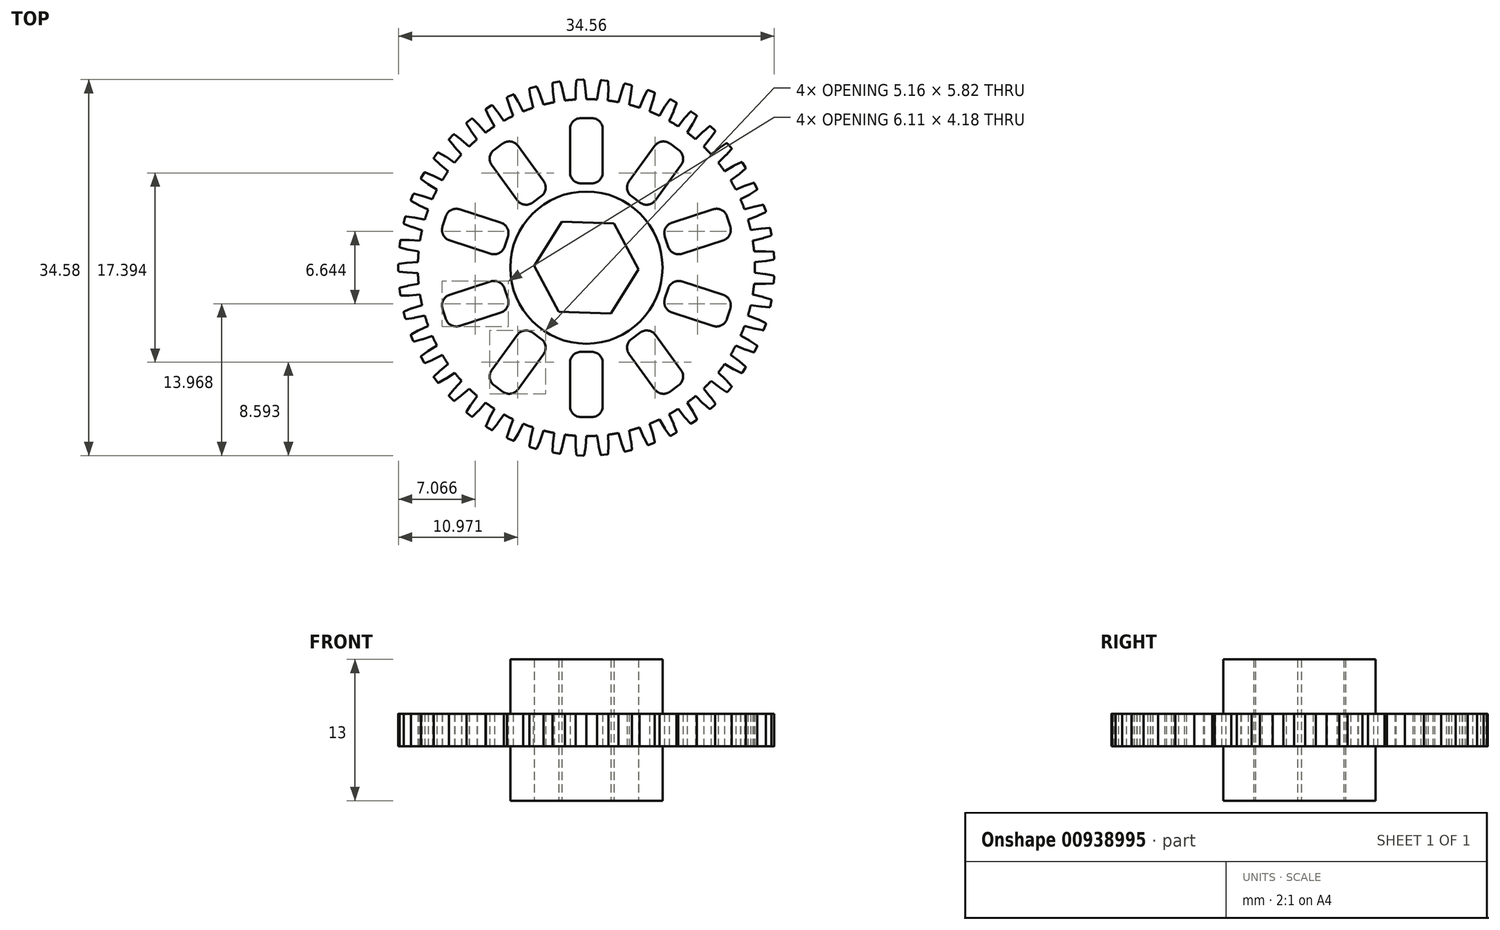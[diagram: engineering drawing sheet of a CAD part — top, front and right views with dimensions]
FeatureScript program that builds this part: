
annotation { "Feature Type Name" : "Feature", "Feature Type Description" : "" }
export const myFeature = defineFeature(function(context is Context, id is Id, definition is map)
    precondition{}
    {
        {
            var Q0;
            Q0=qCreatedBy(makeId("Top.planeOp"),FACE);
            var sketch = newSketch(context, id + "F0", { "sketchPlane" : qUnion([Q0])});
            skCircle(sketch, "E0", {"center": v(0, 0) * mm, "radius": 7 * mm});
            skArc(sketch, "E1", {"start": v(-1, 15.47) * mm, "mid": v(0.5, -15.5) * mm, "end": v(0, 15.5) * mm});
            skCircle(sketch, "E2", {"center": v(0, 0) * mm, "radius": 14.5 * mm});
            skLineSegment(sketch, "E3", {"start": v(-1, 15.47) * mm, "end": v(0, 15.5) * mm});
            skPoint(sketch, "E4.0.midPoint", {"position": v(-3.35, 1.99) * mm});
            skCircle(sketch, "E5.cCircle", {"center": v(0, 0) * mm, "radius": 4.15 * mm, "construction": true});
            skLineSegment(sketch, "E5.0", {"start": v(-4.79, 0.17) * mm, "end": v(-2.25, 4.23) * mm});
            skLineSegment(sketch, "E5.1", {"start": v(-2.25, 4.23) * mm, "end": v(2.54, 4.06) * mm});
            skLineSegment(sketch, "E5.2", {"start": v(2.54, 4.06) * mm, "end": v(4.79, -0.17) * mm});
            skLineSegment(sketch, "E5.3", {"start": v(4.79, -0.17) * mm, "end": v(2.25, -4.23) * mm});
            skLineSegment(sketch, "E5.4", {"start": v(2.25, -4.23) * mm, "end": v(-2.54, -4.06) * mm});
            skLineSegment(sketch, "E5.5", {"start": v(-2.54, -4.06) * mm, "end": v(-4.79, 0.17) * mm});
            skPoint(sketch, "E5.0.midPoint", {"position": v(-3.52, 2.2) * mm});
            skPoint(sketch, "E6.orphan", {"position": v(-2.3, -3.87) * mm});
            skPoint(sketch, "E7.orphan", {"position": v(2.2, -3.92) * mm});
            skPoint(sketch, "E8.orphan", {"position": v(-4.5, 0.05) * mm});
            skPoint(sketch, "E4.1.start.orphan", {"position": v(-2.2, 3.92) * mm});
            skLineSegment(sketch, "E9", {"start": v(-0.5, 15.48) * mm, "end": v(-0.53, 16.48) * mm});
            skLineSegment(sketch, "E10", {"start": v(-0.53, 16.48) * mm, "end": v(-0.98, 16.47) * mm});
            skLineSegment(sketch, "E11", {"start": v(-0.98, 16.47) * mm, "end": v(-0.08, 16.5) * mm});
            skLineSegment(sketch, "E12", {"start": v(-0.98, 16.45) * mm, "end": v(-1, 15.47) * mm});
            skLineSegment(sketch, "E13", {"start": v(-0.08, 16.48) * mm, "end": v(0, 15.5) * mm});
            skLineSegment(sketch, "E14", {"start": v(-0.53, 16.48) * mm, "end": v(-0.56, 17.28) * mm});
            skLineSegment(sketch, "E15", {"start": v(-0.56, 17.28) * mm, "end": v(-0.82, 17.27) * mm});
            skLineSegment(sketch, "E16", {"start": v(-0.82, 17.27) * mm, "end": v(-0.3, 17.3) * mm});
            skLineSegment(sketch, "E17", {"start": v(-0.92, 17.18) * mm, "end": v(-0.98, 16.49) * mm});
            skLineSegment(sketch, "E18", {"start": v(-0.2, 17.2) * mm, "end": v(-0.09, 16.52) * mm});
            skPoint(sketch, "E19.visualSharp", {"position": v(-0.2, 17.3) * mm});
            skArc(sketch, "E19.filletArc", {"start": v(-0.2, 17.2) * mm, "mid": v(-0.23, 17.27) * mm, "end": v(-0.3, 17.3) * mm});
            skPoint(sketch, "E20.visualSharp", {"position": v(-0.9, 17.27) * mm});
            skArc(sketch, "E20.filletArc", {"start": v(-0.82, 17.27) * mm, "mid": v(-0.88, 17.25) * mm, "end": v(-0.92, 17.18) * mm});
            skPoint(sketch, "E21.visualSharp", {"position": v(-0.08, 16.5) * mm});
            skArc(sketch, "E21.filletArc", {"start": v(-0.08, 16.48) * mm, "mid": v(-0.08, 16.5) * mm, "end": v(-0.09, 16.52) * mm});
            skPoint(sketch, "E22.visualSharp", {"position": v(-0.98, 16.47) * mm});
            skArc(sketch, "E22.filletArc", {"start": v(-0.98, 16.49) * mm, "mid": v(-0.98, 16.47) * mm, "end": v(-0.98, 16.45) * mm});
            skPoint(sketch, "E23", {"position": v(0, 7) * mm});
            skPoint(sketch, "E24", {"position": v(0, 14.5) * mm});
            skPoint(sketch, "E25", {"position": v(0, 10.75) * mm});
            skLineSegment(sketch, "E26.bottom", {"start": v(0.5, 13.75) * mm, "end": v(-0.5, 13.75) * mm});
            skLineSegment(sketch, "E26.top", {"start": v(0.5, 7.75) * mm, "end": v(-0.5, 7.75) * mm});
            skLineSegment(sketch, "E26.left", {"start": v(1.5, 12.75) * mm, "end": v(1.5, 8.75) * mm});
            skLineSegment(sketch, "E26.right", {"start": v(-1.5, 12.75) * mm, "end": v(-1.5, 8.75) * mm});
            skPoint(sketch, "E27.visualSharp", {"position": v(-1.5, 13.75) * mm});
            skArc(sketch, "E27.filletArc", {"start": v(-0.5, 13.75) * mm, "mid": v(-1.2, 13.46) * mm, "end": v(-1.5, 12.75) * mm});
            skPoint(sketch, "E28.visualSharp", {"position": v(1.5, 13.75) * mm});
            skArc(sketch, "E28.filletArc", {"start": v(1.5, 12.75) * mm, "mid": v(1.2, 13.46) * mm, "end": v(0.5, 13.75) * mm});
            skPoint(sketch, "E29.visualSharp", {"position": v(1.5, 7.75) * mm});
            skArc(sketch, "E29.filletArc", {"start": v(0.5, 7.75) * mm, "mid": v(1.2, 8.04) * mm, "end": v(1.5, 8.75) * mm});
            skPoint(sketch, "E30.visualSharp", {"position": v(-1.5, 7.75) * mm});
            skArc(sketch, "E30.filletArc", {"start": v(-1.5, 8.75) * mm, "mid": v(-1.2, 8.04) * mm, "end": v(-0.5, 7.75) * mm});
            skLineSegment(sketch, "E31.1.0", {"start": v(-7.68, 11.42) * mm, "end": v(-8.49, 10.83) * mm});
            skArc(sketch, "E31.1.1", {"start": v(-6.28, 11.2) * mm, "mid": v(-6.93, 11.6) * mm, "end": v(-7.68, 11.42) * mm});
            skLineSegment(sketch, "E31.1.2", {"start": v(-6.28, 11.2) * mm, "end": v(-3.93, 7.96) * mm});
            skArc(sketch, "E31.1.3", {"start": v(-4.15, 6.56) * mm, "mid": v(-3.75, 7.22) * mm, "end": v(-3.93, 7.96) * mm});
            skLineSegment(sketch, "E31.1.4", {"start": v(-4.15, 6.56) * mm, "end": v(-4.96, 5.98) * mm});
            skArc(sketch, "E31.1.5", {"start": v(-6.36, 6.2) * mm, "mid": v(-5.7, 5.8) * mm, "end": v(-4.96, 5.98) * mm});
            skLineSegment(sketch, "E31.1.6", {"start": v(-8.7, 9.43) * mm, "end": v(-6.36, 6.2) * mm});
            skArc(sketch, "E31.1.7", {"start": v(-8.49, 10.83) * mm, "mid": v(-8.89, 10.18) * mm, "end": v(-8.7, 9.43) * mm});
            skLineSegment(sketch, "E31.2.0", {"start": v(-12.92, 4.72) * mm, "end": v(-13.23, 3.77) * mm});
            skArc(sketch, "E31.2.1", {"start": v(-11.66, 5.37) * mm, "mid": v(-12.43, 5.3) * mm, "end": v(-12.92, 4.72) * mm});
            skLineSegment(sketch, "E31.2.2", {"start": v(-11.66, 5.37) * mm, "end": v(-7.86, 4.13) * mm});
            skArc(sketch, "E31.2.3", {"start": v(-7.22, 2.87) * mm, "mid": v(-7.28, 3.63) * mm, "end": v(-7.86, 4.13) * mm});
            skLineSegment(sketch, "E31.2.4", {"start": v(-7.22, 2.87) * mm, "end": v(-7.53, 1.92) * mm});
            skArc(sketch, "E31.2.5", {"start": v(-8.79, 1.28) * mm, "mid": v(-8.02, 1.34) * mm, "end": v(-7.53, 1.92) * mm});
            skLineSegment(sketch, "E31.2.6", {"start": v(-12.59, 2.51) * mm, "end": v(-8.79, 1.28) * mm});
            skArc(sketch, "E31.2.7", {"start": v(-13.23, 3.77) * mm, "mid": v(-13.17, 3.01) * mm, "end": v(-12.59, 2.51) * mm});
            skLineSegment(sketch, "E31.3.0", {"start": v(-13.23, -3.77) * mm, "end": v(-12.92, -4.72) * mm});
            skArc(sketch, "E31.3.1", {"start": v(-12.59, -2.51) * mm, "mid": v(-13.17, -3.01) * mm, "end": v(-13.23, -3.77) * mm});
            skLineSegment(sketch, "E31.3.2", {"start": v(-12.59, -2.51) * mm, "end": v(-8.79, -1.28) * mm});
            skArc(sketch, "E31.3.3", {"start": v(-7.53, -1.92) * mm, "mid": v(-8.02, -1.34) * mm, "end": v(-8.79, -1.28) * mm});
            skLineSegment(sketch, "E31.3.4", {"start": v(-7.53, -1.92) * mm, "end": v(-7.22, -2.87) * mm});
            skArc(sketch, "E31.3.5", {"start": v(-7.86, -4.13) * mm, "mid": v(-7.28, -3.63) * mm, "end": v(-7.22, -2.87) * mm});
            skLineSegment(sketch, "E31.3.6", {"start": v(-11.66, -5.37) * mm, "end": v(-7.86, -4.13) * mm});
            skArc(sketch, "E31.3.7", {"start": v(-12.92, -4.72) * mm, "mid": v(-12.43, -5.3) * mm, "end": v(-11.66, -5.37) * mm});
            skLineSegment(sketch, "E31.4.0", {"start": v(-8.49, -10.83) * mm, "end": v(-7.68, -11.42) * mm});
            skArc(sketch, "E31.4.1", {"start": v(-8.7, -9.43) * mm, "mid": v(-8.89, -10.18) * mm, "end": v(-8.49, -10.83) * mm});
            skLineSegment(sketch, "E31.4.2", {"start": v(-8.7, -9.43) * mm, "end": v(-6.36, -6.2) * mm});
            skArc(sketch, "E31.4.3", {"start": v(-4.96, -5.98) * mm, "mid": v(-5.7, -5.8) * mm, "end": v(-6.36, -6.2) * mm});
            skLineSegment(sketch, "E31.4.4", {"start": v(-4.96, -5.98) * mm, "end": v(-4.15, -6.56) * mm});
            skArc(sketch, "E31.4.5", {"start": v(-3.93, -7.96) * mm, "mid": v(-3.75, -7.22) * mm, "end": v(-4.15, -6.56) * mm});
            skLineSegment(sketch, "E31.4.6", {"start": v(-6.28, -11.2) * mm, "end": v(-3.93, -7.96) * mm});
            skArc(sketch, "E31.4.7", {"start": v(-7.68, -11.42) * mm, "mid": v(-6.93, -11.6) * mm, "end": v(-6.28, -11.2) * mm});
            skLineSegment(sketch, "E31.5.0", {"start": v(-0.5, -13.75) * mm, "end": v(0.5, -13.75) * mm});
            skArc(sketch, "E31.5.1", {"start": v(-1.5, -12.75) * mm, "mid": v(-1.2, -13.46) * mm, "end": v(-0.5, -13.75) * mm});
            skLineSegment(sketch, "E31.5.2", {"start": v(-1.5, -12.75) * mm, "end": v(-1.5, -8.75) * mm});
            skArc(sketch, "E31.5.3", {"start": v(-0.5, -7.75) * mm, "mid": v(-1.2, -8.04) * mm, "end": v(-1.5, -8.75) * mm});
            skLineSegment(sketch, "E31.5.4", {"start": v(-0.5, -7.75) * mm, "end": v(0.5, -7.75) * mm});
            skArc(sketch, "E31.5.5", {"start": v(1.5, -8.75) * mm, "mid": v(1.2, -8.04) * mm, "end": v(0.5, -7.75) * mm});
            skLineSegment(sketch, "E31.5.6", {"start": v(1.5, -12.75) * mm, "end": v(1.5, -8.75) * mm});
            skArc(sketch, "E31.5.7", {"start": v(0.5, -13.75) * mm, "mid": v(1.2, -13.46) * mm, "end": v(1.5, -12.75) * mm});
            skLineSegment(sketch, "E31.6.0", {"start": v(7.68, -11.42) * mm, "end": v(8.49, -10.83) * mm});
            skArc(sketch, "E31.6.1", {"start": v(6.28, -11.2) * mm, "mid": v(6.93, -11.6) * mm, "end": v(7.68, -11.42) * mm});
            skLineSegment(sketch, "E31.6.2", {"start": v(6.28, -11.2) * mm, "end": v(3.93, -7.96) * mm});
            skArc(sketch, "E31.6.3", {"start": v(4.15, -6.56) * mm, "mid": v(3.75, -7.22) * mm, "end": v(3.93, -7.96) * mm});
            skLineSegment(sketch, "E31.6.4", {"start": v(4.15, -6.56) * mm, "end": v(4.96, -5.98) * mm});
            skArc(sketch, "E31.6.5", {"start": v(6.36, -6.2) * mm, "mid": v(5.7, -5.8) * mm, "end": v(4.96, -5.98) * mm});
            skLineSegment(sketch, "E31.6.6", {"start": v(8.7, -9.43) * mm, "end": v(6.36, -6.2) * mm});
            skArc(sketch, "E31.6.7", {"start": v(8.49, -10.83) * mm, "mid": v(8.89, -10.18) * mm, "end": v(8.7, -9.43) * mm});
            skLineSegment(sketch, "E31.7.0", {"start": v(12.92, -4.72) * mm, "end": v(13.23, -3.77) * mm});
            skArc(sketch, "E31.7.1", {"start": v(11.66, -5.37) * mm, "mid": v(12.43, -5.3) * mm, "end": v(12.92, -4.72) * mm});
            skLineSegment(sketch, "E31.7.2", {"start": v(11.66, -5.37) * mm, "end": v(7.86, -4.13) * mm});
            skArc(sketch, "E31.7.3", {"start": v(7.22, -2.87) * mm, "mid": v(7.28, -3.63) * mm, "end": v(7.86, -4.13) * mm});
            skLineSegment(sketch, "E31.7.4", {"start": v(7.22, -2.87) * mm, "end": v(7.53, -1.92) * mm});
            skArc(sketch, "E31.7.5", {"start": v(8.79, -1.28) * mm, "mid": v(8.02, -1.34) * mm, "end": v(7.53, -1.92) * mm});
            skLineSegment(sketch, "E31.7.6", {"start": v(12.59, -2.51) * mm, "end": v(8.79, -1.28) * mm});
            skArc(sketch, "E31.7.7", {"start": v(13.23, -3.77) * mm, "mid": v(13.17, -3.01) * mm, "end": v(12.59, -2.51) * mm});
            skLineSegment(sketch, "E31.8.0", {"start": v(13.23, 3.77) * mm, "end": v(12.92, 4.72) * mm});
            skArc(sketch, "E31.8.1", {"start": v(12.59, 2.51) * mm, "mid": v(13.17, 3.01) * mm, "end": v(13.23, 3.77) * mm});
            skLineSegment(sketch, "E31.8.2", {"start": v(12.59, 2.51) * mm, "end": v(8.79, 1.28) * mm});
            skArc(sketch, "E31.8.3", {"start": v(7.53, 1.92) * mm, "mid": v(8.02, 1.34) * mm, "end": v(8.79, 1.28) * mm});
            skLineSegment(sketch, "E31.8.4", {"start": v(7.53, 1.92) * mm, "end": v(7.22, 2.87) * mm});
            skArc(sketch, "E31.8.5", {"start": v(7.86, 4.13) * mm, "mid": v(7.28, 3.63) * mm, "end": v(7.22, 2.87) * mm});
            skLineSegment(sketch, "E31.8.6", {"start": v(11.66, 5.37) * mm, "end": v(7.86, 4.13) * mm});
            skArc(sketch, "E31.8.7", {"start": v(12.92, 4.72) * mm, "mid": v(12.43, 5.3) * mm, "end": v(11.66, 5.37) * mm});
            skLineSegment(sketch, "E31.9.0", {"start": v(8.49, 10.83) * mm, "end": v(7.68, 11.42) * mm});
            skArc(sketch, "E31.9.1", {"start": v(8.7, 9.43) * mm, "mid": v(8.89, 10.18) * mm, "end": v(8.49, 10.83) * mm});
            skLineSegment(sketch, "E31.9.2", {"start": v(8.7, 9.43) * mm, "end": v(6.36, 6.2) * mm});
            skArc(sketch, "E31.9.3", {"start": v(4.96, 5.98) * mm, "mid": v(5.7, 5.8) * mm, "end": v(6.36, 6.2) * mm});
            skLineSegment(sketch, "E31.9.4", {"start": v(4.96, 5.98) * mm, "end": v(4.15, 6.56) * mm});
            skArc(sketch, "E31.9.5", {"start": v(3.93, 7.96) * mm, "mid": v(3.75, 7.22) * mm, "end": v(4.15, 6.56) * mm});
            skLineSegment(sketch, "E31.9.6", {"start": v(6.28, 11.2) * mm, "end": v(3.93, 7.96) * mm});
            skArc(sketch, "E31.9.7", {"start": v(7.68, 11.42) * mm, "mid": v(6.93, 11.6) * mm, "end": v(6.28, 11.2) * mm});
            skSolve(sketch);
        }
        {
            var Q0;
            Q0=qCreatedBy(makeId("Front.planeOp"),FACE);
            var sketch = newSketch(context, id + "F1", { "sketchPlane" : qUnion([Q0])});
            skLineSegment(sketch, "E32", {"start": v(0, 0) * mm, "end": v(0, 26.77) * mm, "construction": true});
            skSolve(sketch);
        }
        {
            var Q0;
            Q0=makeQuery(id+"F0.imprint","IMPRINT",FACE,{"disambiguationData":[TD([[makeQuery(id+"F0.imprint","IMPRINT",EDGE,{"derivedFrom":sQuery(id+"F0.wireOp",EDGE,"E0")}),1.0]])]});
            extrude(context, id + "F2", {"entities" : qUnion([Q0]), "depth" : 13 * mm, "offsetDistance" : 25 * mm, "symmetric" : true});
        }
        {
            var Q0;
            Q0=makeQuery(id+"F0.imprint","IMPRINT",FACE,{"disambiguationData":[TD([[makeQuery(id+"F0.imprint","IMPRINT",EDGE,{"derivedFrom":sQuery(id+"F0.wireOp",EDGE,"E0")}),-1.0]])]});
            extrude(context, id + "F3", {"entities" : qUnion([Q0]), "operationType" : NewBodyOperationType.ADD, "depth" : 3 * mm, "offsetDistance" : 25 * mm, "symmetric" : true});
        }
        {
            var Q0;
            Q0=makeQuery(id+"F0.imprint","IMPRINT",FACE,{"disambiguationData":[TD([[makeQuery(id+"F0.imprint","IMPRINT",EDGE,{"derivedFrom":sQuery(id+"F0.wireOp",EDGE,"E2")}),-1.0]])]});
            extrude(context, id + "F4", {"entities" : qUnion([Q0]), "operationType" : NewBodyOperationType.ADD, "depth" : 3 * mm, "offsetDistance" : 25 * mm, "symmetric" : true});
        }
        {
            var Q0;
            {var subQ2=sQuery(id+"F0.wireOp",EDGE,"E9");Q0=makeQuery(id+"F0.imprint","IMPRINT",FACE,{"disambiguationData":[TD([[makeQuery(id+"F0.imprint","IMPRINT",EDGE,{"derivedFrom":subQ2}),1.0]])]});}
            var Q1;
            {var subQ2=sQuery(id+"F0.wireOp",EDGE,"E9");Q1=makeQuery(id+"F0.imprint","IMPRINT",FACE,{"disambiguationData":[TD([[makeQuery(id+"F0.imprint","IMPRINT",EDGE,{"derivedFrom":subQ2}),-1.0]])]});}
            var Q2;
            {var subQ1=sQuery(id+"F0.wireOp",EDGE,"E14");Q2=makeQuery(id+"F0.imprint","IMPRINT",FACE,{"disambiguationData":[TD([[makeQuery(id+"F0.imprint","IMPRINT",EDGE,{"derivedFrom":subQ1}),-1.0]])]});}
            var Q3;
            {var subQ1=sQuery(id+"F0.wireOp",EDGE,"E14");Q3=makeQuery(id+"F0.imprint","IMPRINT",FACE,{"disambiguationData":[TD([[makeQuery(id+"F0.imprint","IMPRINT",EDGE,{"derivedFrom":subQ1}),1.0]])]});}
            extrude(context, id + "F5", {"entities" : qUnion([Q0, Q1, Q2, Q3]), "depth" : 3 * mm, "offsetDistance" : 25 * mm, "symmetric" : true});
        }
        {
            var Q0;
            Q0=makeQuery(id+"F5.opExtrude","SWEPT_BODY",BODY,{"disambiguationData":[OSD([sQuery(id+"F0.wireOp",EDGE,"E3"),sQuery(id+"F0.wireOp",EDGE,"zY2qvlCe-LwUi-iNXd-wZ7Z-H6Lx6uWpxhC7"),sQuery(id+"F0.wireOp",EDGE,"CL1w9jXF-FcO4-JGJ7-eMMN-SI9SSlm3FFuX")])]});
            var Q1;
            Q1=sQuery(id+"F1.wireOp",EDGE,"E32");
            circularPattern(context, id + "F6", {"operationType" : NewBodyOperationType.ADD, "entities" : qUnion([Q0]), "axis" : qUnion([Q1]), "angle" : 360 * degree, "instanceCount" : 49, "equalSpace" : true});
        }
    });
